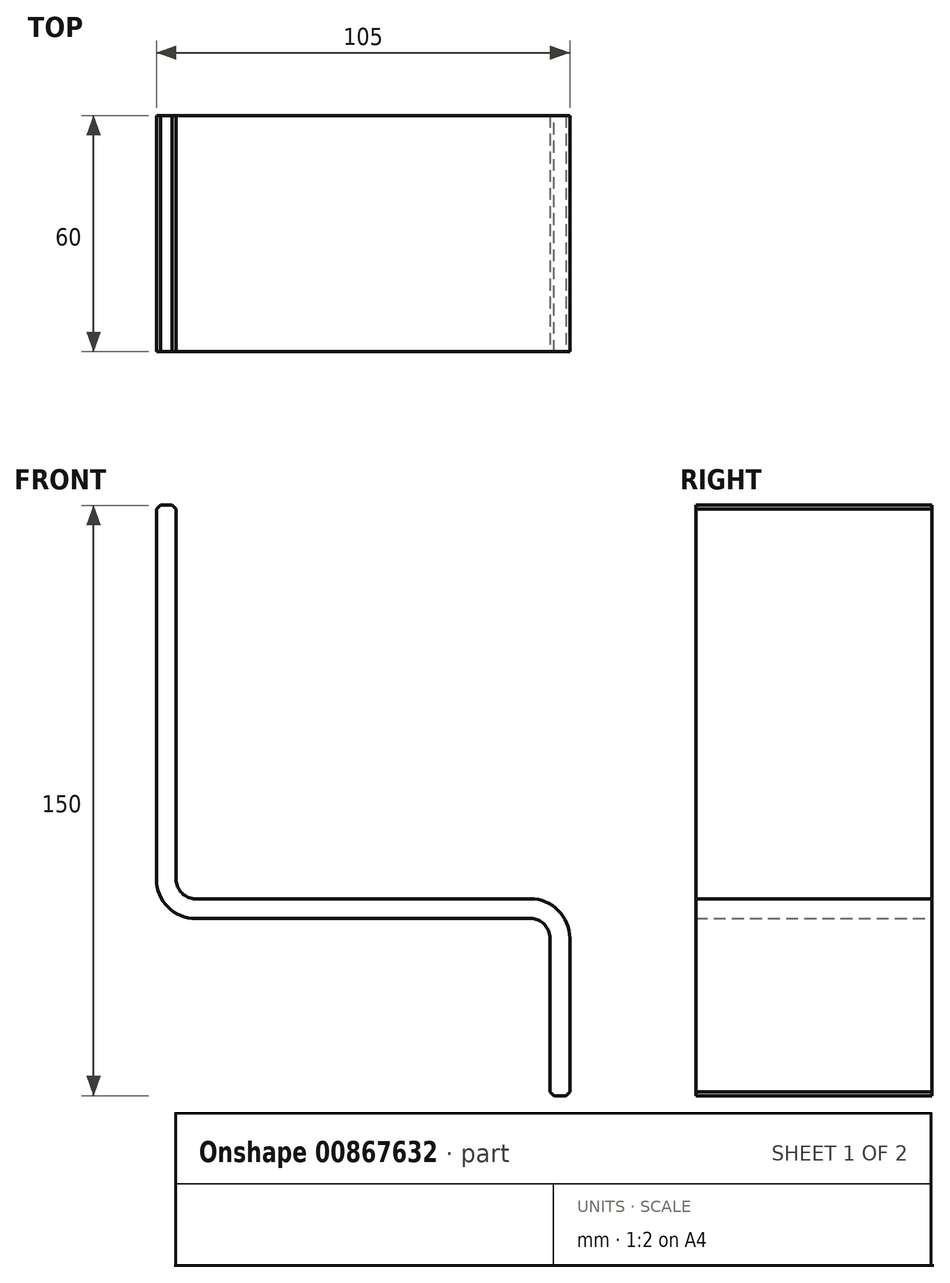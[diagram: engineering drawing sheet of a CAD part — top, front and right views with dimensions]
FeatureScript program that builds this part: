
annotation { "Feature Type Name" : "Feature", "Feature Type Description" : "" }
export const myFeature = defineFeature(function(context is Context, id is Id, definition is map)
    precondition{}
    {
        {
            var Q0;
            Q0=qCreatedBy(makeId("Front.planeOp"),FACE);
            var sketch = newSketch(context, id + "F0", { "sketchPlane" : qUnion([Q0])});
            skLineSegment(sketch, "E0", {"start": v(-45.24, 63.1) * mm, "end": v(-45.24, -36.9) * mm});
            skLineSegment(sketch, "E1", {"start": v(-45.24, -36.9) * mm, "end": v(54.76, -36.9) * mm});
            skLineSegment(sketch, "E2", {"start": v(54.76, -36.9) * mm, "end": v(54.76, -86.9) * mm});
            skLineSegment(sketch, "E3", {"start": v(-45.24, 63.1) * mm, "end": v(-50.24, 63.1) * mm});
            skLineSegment(sketch, "E4", {"start": v(-50.24, 63.1) * mm, "end": v(-50.24, -41.9) * mm});
            skLineSegment(sketch, "E5", {"start": v(-50.24, -41.9) * mm, "end": v(49.76, -41.9) * mm});
            skLineSegment(sketch, "E6", {"start": v(49.76, -41.9) * mm, "end": v(49.76, -86.9) * mm});
            skLineSegment(sketch, "E7", {"start": v(49.76, -86.9) * mm, "end": v(54.76, -86.9) * mm});
            skSolve(sketch);
        }
        {
            var Q0;
            Q0=makeQuery(id+"F0.imprint","IMPRINT",FACE,{"disambiguationData":[TD([[makeQuery(id+"F0.imprint","IMPRINT",EDGE,{"derivedFrom":sQuery(id+"F0.wireOp",EDGE,"E0")}),-1.0]])]});
            extrude(context, id + "F1", {"entities" : qUnion([Q0]), "depth" : 60 * mm, "offsetDistance" : 25 * mm});
        }
        {
            var Q0;
            Q0=makeQuery(id+"F1.opExtrude","SWEPT_EDGE",EDGE,{"disambiguationData":[OSD([sQuery(id+"F0.wireOp",EDGE,"E0"),sQuery(id+"F0.wireOp",EDGE,"E1")])]});
            var Q1;
            Q1=makeQuery(id+"F1.opExtrude","SWEPT_EDGE",EDGE,{"disambiguationData":[OSD([sQuery(id+"F0.wireOp",EDGE,"E5"),sQuery(id+"F0.wireOp",EDGE,"E6")])]});
            fillet(context, id + "F2", {"entities" : qUnion([Q0, Q1]), "radius" : 5 * mm, "tangentPropagation" : true, "allowEdgeOverflow" : false});
        }
        {
            var Q0;
            Q0=makeQuery(id+"F1.opExtrude","SWEPT_EDGE",EDGE,{"disambiguationData":[OSD([sQuery(id+"F0.wireOp",EDGE,"E1"),sQuery(id+"F0.wireOp",EDGE,"E2")])]});
            var Q1;
            Q1=makeQuery(id+"F1.opExtrude","SWEPT_EDGE",EDGE,{"disambiguationData":[OSD([sQuery(id+"F0.wireOp",EDGE,"E4"),sQuery(id+"F0.wireOp",EDGE,"E5")])]});
            fillet(context, id + "F3", {"entities" : qUnion([Q0, Q1]), "radius" : 10 * mm, "tangentPropagation" : true, "allowEdgeOverflow" : false});
        }
        {
            var Q0;
            Q0=makeQuery(id+"F1.opExtrude","SWEPT_EDGE",EDGE,{"disambiguationData":[OSD([sQuery(id+"F0.wireOp",EDGE,"E0"),sQuery(id+"F0.wireOp",EDGE,"E3")])]});
            var Q1;
            Q1=makeQuery(id+"F1.opExtrude","SWEPT_EDGE",EDGE,{"disambiguationData":[OSD([sQuery(id+"F0.wireOp",EDGE,"E3"),sQuery(id+"F0.wireOp",EDGE,"E4")])]});
            var Q2;
            Q2=makeQuery(id+"F1.opExtrude","SWEPT_EDGE",EDGE,{"disambiguationData":[OSD([sQuery(id+"F0.wireOp",EDGE,"E2"),sQuery(id+"F0.wireOp",EDGE,"E7")])]});
            var Q3;
            Q3=makeQuery(id+"F1.opExtrude","SWEPT_EDGE",EDGE,{"disambiguationData":[OSD([sQuery(id+"F0.wireOp",EDGE,"E6"),sQuery(id+"F0.wireOp",EDGE,"E7")])]});
            chamfer(context, id + "F4", {"entities" : qUnion([Q0, Q1, Q2, Q3]), "width" : 1 * mm, "tangentPropagation" : true});
        }
    });
